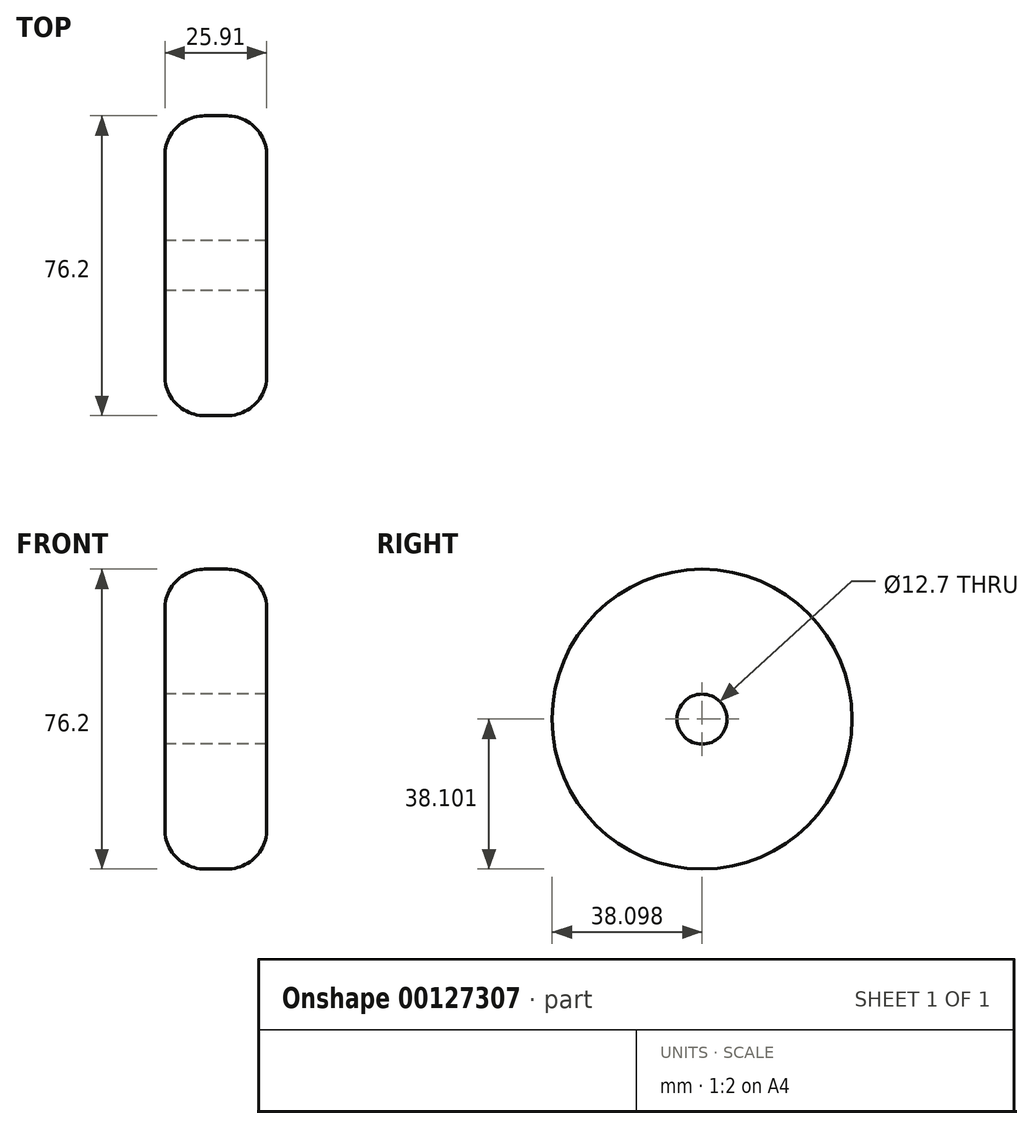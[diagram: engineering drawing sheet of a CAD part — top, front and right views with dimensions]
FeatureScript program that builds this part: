
annotation { "Feature Type Name" : "Feature", "Feature Type Description" : "" }
export const myFeature = defineFeature(function(context is Context, id is Id, definition is map)
    precondition{}
    {
        {
            var Q0;
            Q0=qCreatedBy(makeId("Right.planeOp"),FACE);
            var sketch = newSketch(context, id + "F0", { "sketchPlane" : qUnion([Q0])});
            skCircle(sketch, "E0", {"center": v(0.19, 0.47) * mm, "radius": 38.1 * mm});
            skCircle(sketch, "E1", {"center": v(0.19, 0.47) * mm, "radius": 6.35 * mm});
            skSolve(sketch);
        }
        {
            var Q0;
            Q0 = qSketchRegion(id + "F0", true);
            extrude(context, id + "F1", {"entities" : qUnion([Q0]), "depth" : 25.9 * mm});
        }
        {
            var Q0;
            Q0=makeQuery(id+"F1.opExtrude","SWEPT_FACE",FACE,{"disambiguationData":[OSD([sQuery(id+"F0.wireOp",EDGE,"E0")])]});
            fillet(context, id + "F2", {"entities" : qUnion([Q0]), "radius" : 10.16 * mm, "tangentPropagation" : true, "allowEdgeOverflow" : false});
        }
    });
